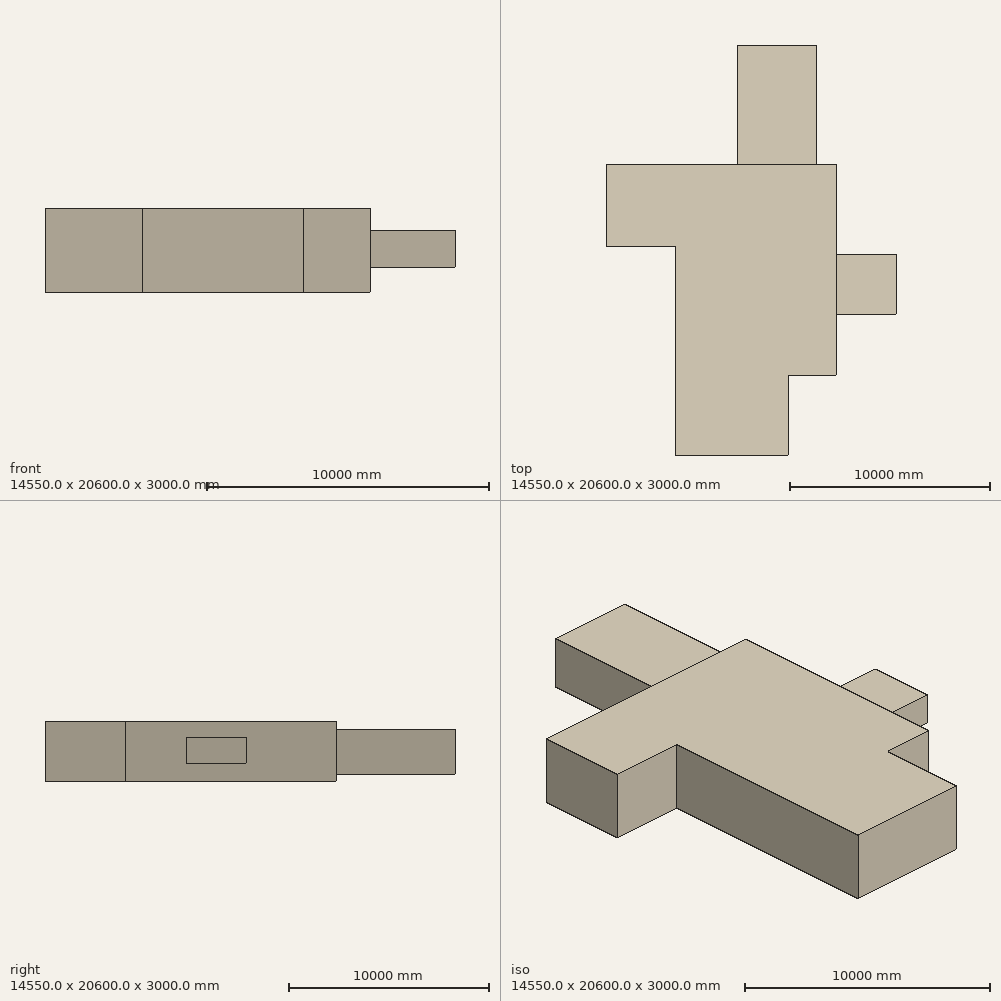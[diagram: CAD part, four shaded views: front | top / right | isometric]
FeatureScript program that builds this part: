
annotation { "Feature Type Name" : "Feature", "Feature Type Description" : "" }
export const myFeature = defineFeature(function(context is Context, id is Id, definition is map)
    precondition{}
    {
        {
            var Q0;
            Q0=qCreatedBy(makeId("Top.planeOp"),FACE);
            var sketch = newSketch(context, id + "F0", { "sketchPlane" : qUnion([Q0])});
            skLineSegment(sketch, "E0", {"start": v(0, 0) * mm, "end": v(11550, 0) * mm});
            skLineSegment(sketch, "E1", {"start": v(11550, 0) * mm, "end": v(11550, -10600) * mm});
            skLineSegment(sketch, "E2", {"start": v(11550, -10600) * mm, "end": v(9150, -10600) * mm});
            skLineSegment(sketch, "E3", {"start": v(9150, -10600) * mm, "end": v(9150, -14600) * mm});
            skLineSegment(sketch, "E4", {"start": v(9150, -14600) * mm, "end": v(3450, -14600) * mm});
            skLineSegment(sketch, "E5", {"start": v(3450, -14600) * mm, "end": v(3450, -4100) * mm});
            skLineSegment(sketch, "E6", {"start": v(3450, -4100) * mm, "end": v(0, -4100) * mm});
            skLineSegment(sketch, "E7", {"start": v(0, -4100) * mm, "end": v(0, 0) * mm});
            skSolve(sketch);
        }
        {
            var Q0;
            Q0 = qSketchRegion(id + "F0", true);
            extrude(context, id + "F1", {"entities" : qUnion([Q0]), "depth" : 3000 * mm, "offsetDistance" : 25 * mm});
        }
        {
            var Q0;
            Q0=makeQuery(id+"F1.opExtrude","SWEPT_FACE",FACE,{"disambiguationData":[OSD([sQuery(id+"F0.wireOp",EDGE,"E1")])]});
            var sketch = newSketch(context, id + "F2", { "sketchPlane" : qUnion([Q0])});
            skLineSegment(sketch, "E8.bottom", {"start": v(-7516.98, 2223.7) * mm, "end": v(-4516.98, 2223.7) * mm});
            skLineSegment(sketch, "E8.top", {"start": v(-7516.98, 896.9) * mm, "end": v(-4516.98, 896.9) * mm});
            skLineSegment(sketch, "E8.left", {"start": v(-7516.98, 2223.7) * mm, "end": v(-7516.98, 896.9) * mm});
            skLineSegment(sketch, "E8.right", {"start": v(-4516.98, 2223.7) * mm, "end": v(-4516.98, 896.9) * mm});
            skSolve(sketch);
        }
        {
            var Q0;
            Q0 = qSketchRegion(id + "F2", true);
            extrude(context, id + "F3", {"entities" : qUnion([Q0]), "operationType" : NewBodyOperationType.ADD, "depth" : 3000 * mm, "offsetDistance" : 25 * mm});
        }
        {
            var Q0;
            Q0=makeQuery(id+"F1.opExtrude","SWEPT_FACE",FACE,{"disambiguationData":[OSD([sQuery(id+"F0.wireOp",EDGE,"E0")])]});
            var sketch = newSketch(context, id + "F4", { "sketchPlane" : qUnion([Q0])});
            skLineSegment(sketch, "E9.bottom", {"start": v(-10550, 2622.12) * mm, "end": v(-6550, 2622.12) * mm});
            skLineSegment(sketch, "E9.top", {"start": v(-10550, 322.4) * mm, "end": v(-6550, 322.4) * mm});
            skLineSegment(sketch, "E9.left", {"start": v(-10550, 2622.12) * mm, "end": v(-10550, 322.4) * mm});
            skLineSegment(sketch, "E9.right", {"start": v(-6550, 2622.12) * mm, "end": v(-6550, 322.4) * mm});
            skSolve(sketch);
        }
        {
            var Q0;
            Q0 = qSketchRegion(id + "F4", true);
            extrude(context, id + "F5", {"entities" : qUnion([Q0]), "operationType" : NewBodyOperationType.ADD, "depth" : 6000 * mm, "offsetDistance" : 25 * mm});
        }
    });
